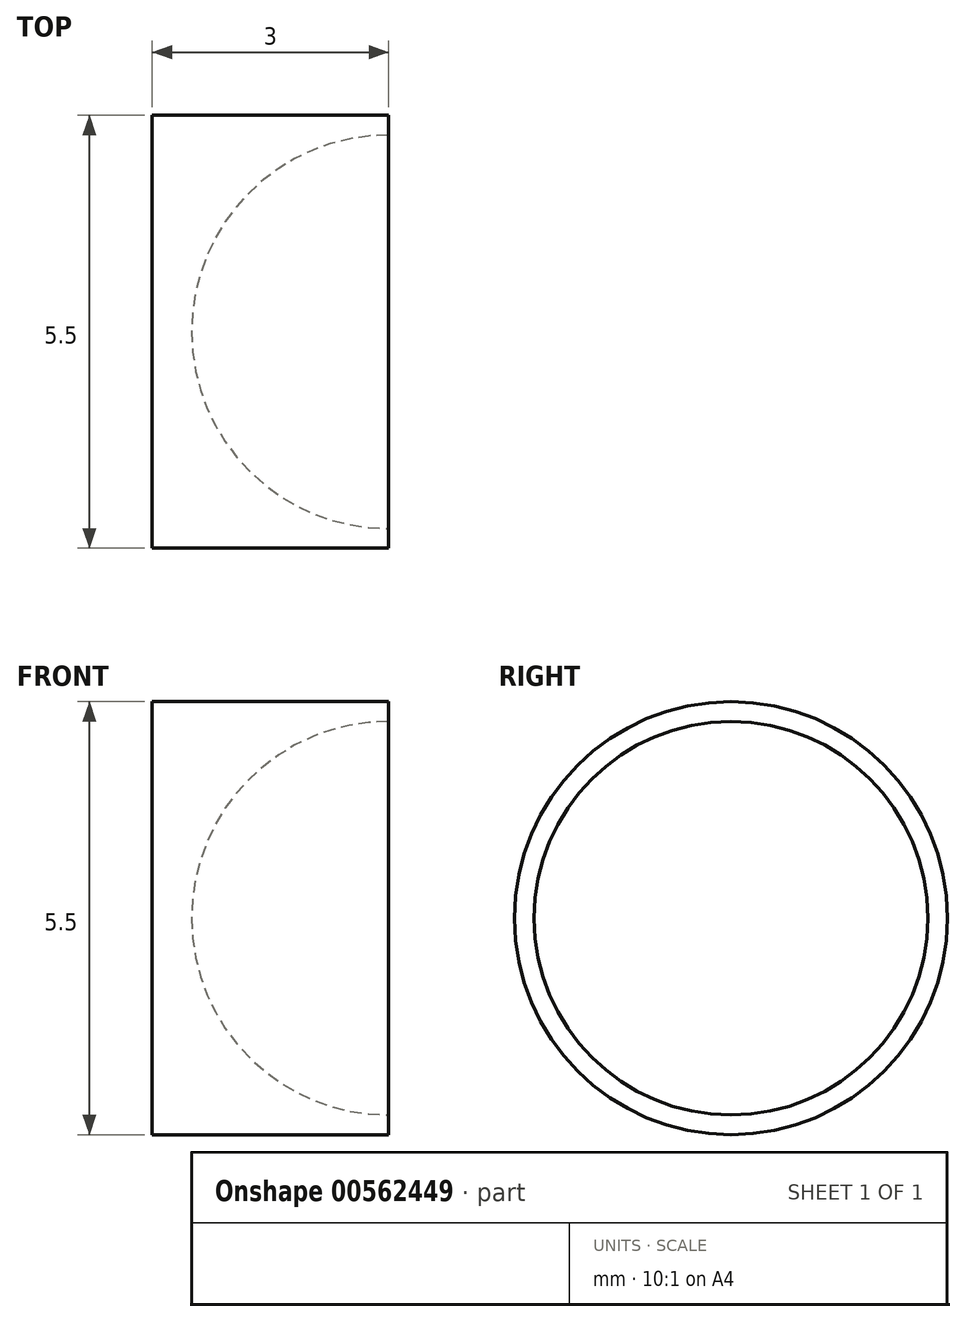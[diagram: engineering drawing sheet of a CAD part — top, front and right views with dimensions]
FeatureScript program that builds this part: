
annotation { "Feature Type Name" : "Feature", "Feature Type Description" : "" }
export const myFeature = defineFeature(function(context is Context, id is Id, definition is map)
    precondition{}
    {
        {
            var Q0;
            Q0=qCreatedBy(makeId("Right.planeOp"),FACE);
            var sketch = newSketch(context, id + "F0", { "sketchPlane" : qUnion([Q0])});
            skCircle(sketch, "E0", {"center": v(0, 0) * mm, "radius": 2.75 * mm});
            skSolve(sketch);
        }
        {
            var Q0;
            Q0 = qSketchRegion(id + "F0", true);
            extrude(context, id + "F1", {"entities" : qUnion([Q0]), "depth" : 3 * mm, "offsetDistance" : 25 * mm});
        }
        {
            var Q0;
            Q0=qCreatedBy(makeId("Top.planeOp"),FACE);
            var sketch = newSketch(context, id + "F2", { "sketchPlane" : qUnion([Q0])});
            skArc(sketch, "E1", {"start": v(3, 2.5) * mm, "mid": v(0.5, 0) * mm, "end": v(3, -2.5) * mm});
            skLineSegment(sketch, "E2", {"start": v(3, 2.5) * mm, "end": v(3, -2.5) * mm});
            skSolve(sketch);
        }
        {
            var Q0;
            Q0 = qSketchRegion(id + "F2", true);
            var Q1;
            Q1=sQuery(id+"F2.wireOp",EDGE,"E2");
            revolve(context, id + "F3", {"operationType" : NewBodyOperationType.REMOVE, "entities" : qUnion([Q0]), "axis" : qUnion([Q1]), "revolveType" : RevolveType.FULL, "oppositeDirection" : true});
        }
    });
